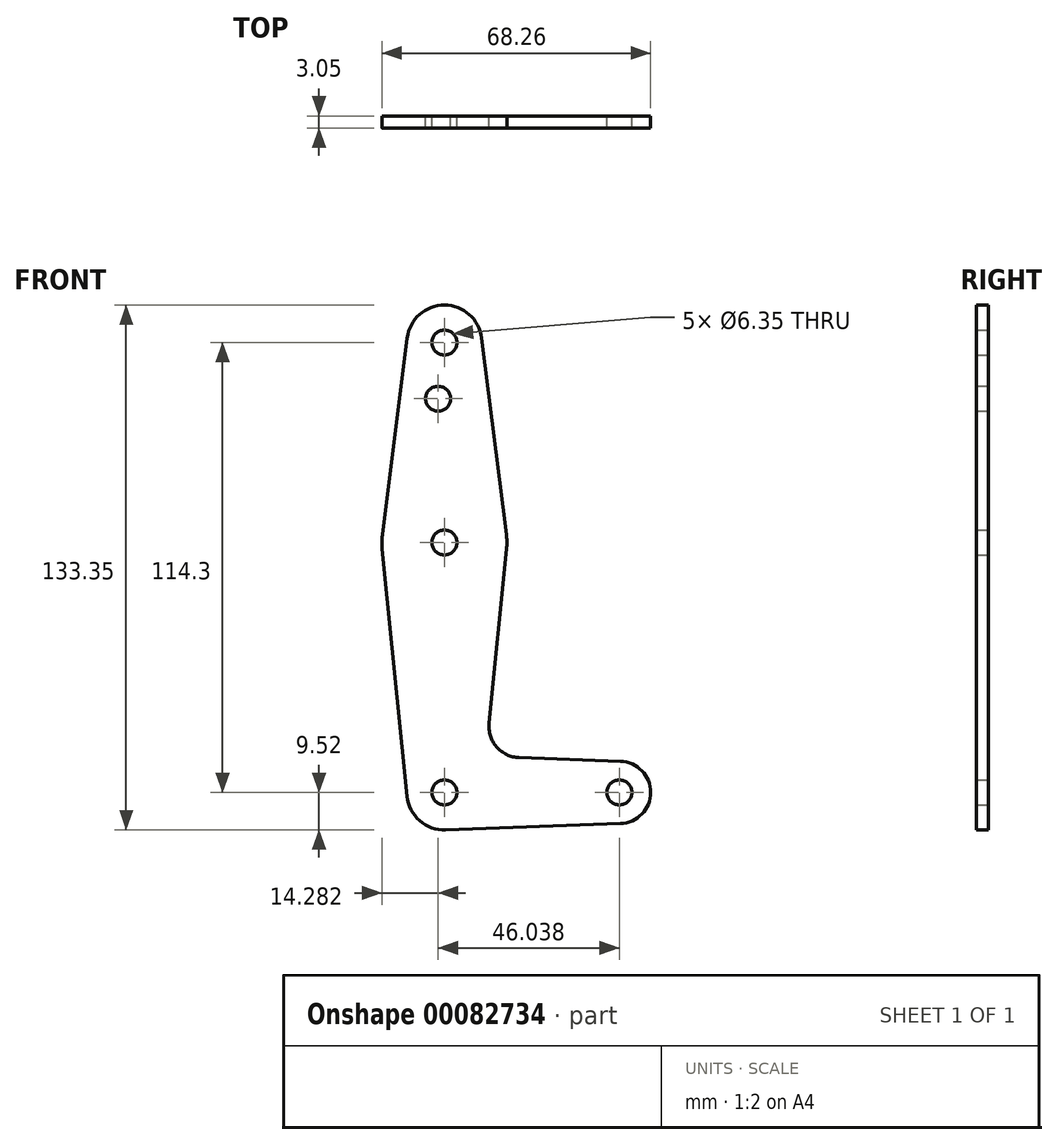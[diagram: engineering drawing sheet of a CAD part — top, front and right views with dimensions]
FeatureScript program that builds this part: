
annotation { "Feature Type Name" : "Feature", "Feature Type Description" : "" }
export const myFeature = defineFeature(function(context is Context, id is Id, definition is map)
    precondition{}
    {
        {
            var Q0;
            Q0=qCreatedBy(makeId("Front.planeOp"),FACE);
            var sketch = newSketch(context, id + "F0", { "sketchPlane" : qUnion([Q0])});
            skLineSegment(sketch, "E0", {"start": v(0, 0) * mm, "end": v(0, 114.3) * mm, "construction": true});
            skCircle(sketch, "E1", {"center": v(0, 114.3) * mm, "radius": 9.53 * mm});
            skCircle(sketch, "E2", {"center": v(0, 0) * mm, "radius": 9.53 * mm});
            skLineSegment(sketch, "E3", {"start": v(0, 0) * mm, "end": v(44.45, 0) * mm, "construction": true});
            skCircle(sketch, "E4", {"center": v(44.45, 0) * mm, "radius": 7.94 * mm});
            skCircle(sketch, "E5", {"center": v(0, 63.5) * mm, "radius": 15.88 * mm});
            skLineSegment(sketch, "E6", {"start": v(18.97, 8.85) * mm, "end": v(44.73, 7.93) * mm});
            skLineSegment(sketch, "E7", {"start": v(0.34, -9.52) * mm, "end": v(44.73, -7.93) * mm});
            skLineSegment(sketch, "E8", {"start": v(9.45, 115.5) * mm, "end": v(15.75, 65.48) * mm});
            skLineSegment(sketch, "E9", {"start": v(-9.45, 115.5) * mm, "end": v(-15.75, 65.48) * mm});
            skLineSegment(sketch, "E10", {"start": v(-9.48, -0.95) * mm, "end": v(-15.8, 61.91) * mm});
            skLineSegment(sketch, "E11", {"start": v(15.8, 61.91) * mm, "end": v(11.34, 17.6) * mm});
            skCircle(sketch, "E12", {"center": v(0, 114.3) * mm, "radius": 3.18 * mm});
            skCircle(sketch, "E13", {"center": v(0, 63.5) * mm, "radius": 3.18 * mm});
            skCircle(sketch, "E14", {"center": v(0, 0) * mm, "radius": 3.18 * mm});
            skCircle(sketch, "E15", {"center": v(44.45, 0) * mm, "radius": 3.18 * mm});
            skArc(sketch, "E16.filletArc", {"start": v(11.34, 17.6) * mm, "mid": v(13.26, 11.57) * mm, "end": v(18.97, 8.85) * mm});
            skCircle(sketch, "E17", {"center": v(-1.59, 100.03) * mm, "radius": 3.18 * mm});
            skSolve(sketch);
        }
        {
            var Q0;
            Q0=makeQuery(id+"F0.imprint","IMPRINT",FACE,{"disambiguationData":[TD([[makeQuery(id+"F0.imprint","IMPRINT",EDGE,{"derivedFrom":sQuery(id+"F0.wireOp",EDGE,"E12")}),-1.0]])]});
            var Q1;
            {var subQ1=sQuery(id+"F0.wireOp",EDGE,"E8");Q1=makeQuery(id+"F0.imprint","IMPRINT",FACE,{"disambiguationData":[TD([[makeQuery(id+"F0.imprint","IMPRINT",EDGE,{"derivedFrom":subQ1}),-1.0]])]});}
            var Q2;
            Q2=makeQuery(id+"F0.imprint","IMPRINT",FACE,{"disambiguationData":[TD([[makeQuery(id+"F0.imprint","IMPRINT",EDGE,{"derivedFrom":sQuery(id+"F0.wireOp",EDGE,"E13")}),-1.0]])]});
            var Q3;
            {var subQ0=sQuery(id+"F0.wireOp",EDGE,"E6");Q3=makeQuery(id+"F0.imprint","IMPRINT",FACE,{"disambiguationData":[TD([[makeQuery(id+"F0.imprint","IMPRINT",EDGE,{"derivedFrom":subQ0}),-1.0]])]});}
            var Q4;
            Q4=makeQuery(id+"F0.imprint","IMPRINT",FACE,{"disambiguationData":[TD([[makeQuery(id+"F0.imprint","IMPRINT",EDGE,{"derivedFrom":sQuery(id+"F0.wireOp",EDGE,"E14")}),-1.0]])]});
            var Q5;
            Q5=makeQuery(id+"F0.imprint","IMPRINT",FACE,{"disambiguationData":[TD([[makeQuery(id+"F0.imprint","IMPRINT",EDGE,{"derivedFrom":sQuery(id+"F0.wireOp",EDGE,"E15")}),-1.0]])]});
            extrude(context, id + "F1", {"entities" : qUnion([Q0, Q1, Q2, Q3, Q4, Q5]), "depth" : 3.05 * mm});
        }
    });
